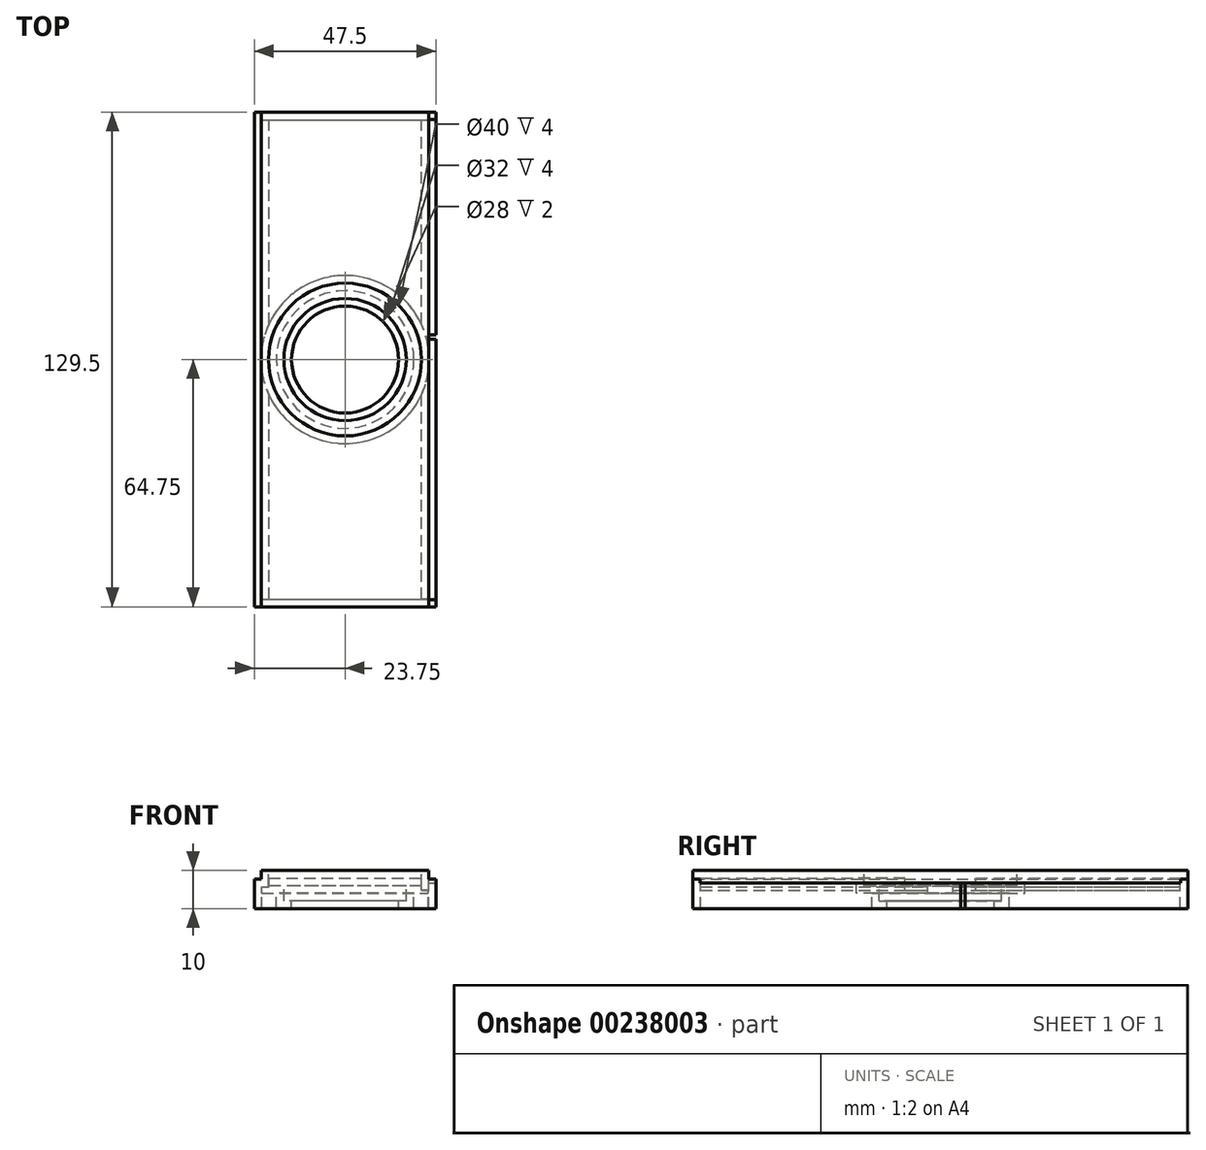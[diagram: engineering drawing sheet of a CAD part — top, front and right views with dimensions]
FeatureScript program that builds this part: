
annotation { "Feature Type Name" : "Feature", "Feature Type Description" : "" }
export const myFeature = defineFeature(function(context is Context, id is Id, definition is map)
    precondition{}
    {
        {
            var Q0;
            Q0=qCreatedBy(makeId("Front.planeOp"),FACE);
            var sketch = newSketch(context, id + "F0", { "sketchPlane" : qUnion([Q0])});
            skLineSegment(sketch, "E0.bottom", {"start": v(-23.75, 0) * mm, "end": v(23.75, 0) * mm});
            skLineSegment(sketch, "E0.top", {"start": v(-23.75, 7.75) * mm, "end": v(-21.95, 7.75) * mm});
            skLineSegment(sketch, "E0.left", {"start": v(-23.75, 0) * mm, "end": v(-23.75, 7.75) * mm});
            skLineSegment(sketch, "E0.right", {"start": v(23.75, 0) * mm, "end": v(23.75, 7.75) * mm});
            skLineSegment(sketch, "E1.top", {"start": v(-21.95, 10) * mm, "end": v(21.95, 10) * mm});
            skLineSegment(sketch, "E1.left", {"start": v(-21.95, 7.75) * mm, "end": v(-21.95, 10) * mm});
            skLineSegment(sketch, "E1.right", {"start": v(21.95, 7.75) * mm, "end": v(21.95, 10) * mm});
            skLineSegment(sketch, "E2.trimOffspring", {"start": v(21.95, 7.75) * mm, "end": v(23.75, 7.75) * mm});
            skSolve(sketch);
        }
        {
            var Q0;
            Q0 = qSketchRegion(id + "F0", true);
            extrude(context, id + "F1", {"entities" : qUnion([Q0]), "endBound" : BoundingType.SYMMETRIC, "depth" : 129.5 * mm});
        }
        {
            var Q0;
            Q0=makeQuery(id+"F1.opExtrude","SWEPT_FACE",FACE,{"disambiguationData":[OSD([sQuery(id+"F0.wireOp",EDGE,"E2.trimOffspring")])]});
            var sketch = newSketch(context, id + "F2", { "sketchPlane" : qUnion([Q0])});
            skLineSegment(sketch, "E3.bottom", {"start": v(23.75, -62.85) * mm, "end": v(21.95, -62.85) * mm});
            skLineSegment(sketch, "E3.top", {"start": v(23.75, 62.85) * mm, "end": v(21.95, 62.85) * mm});
            skLineSegment(sketch, "E3.left", {"start": v(23.75, -62.85) * mm, "end": v(23.75, 62.85) * mm});
            skLineSegment(sketch, "E3.right", {"start": v(21.95, -62.85) * mm, "end": v(21.95, 62.85) * mm});
            skSolve(sketch);
        }
        {
            var Q0;
            Q0 = qSketchRegion(id + "F2", true);
            extrude(context, id + "F3", {"entities" : qUnion([Q0]), "operationType" : NewBodyOperationType.REMOVE, "oppositeDirection" : true, "depth" : 1 * mm});
        }
        {
            var Q0;
            Q0=makeQuery(id+"F1.opExtrude","SWEPT_FACE",FACE,{"disambiguationData":[OSD([sQuery(id+"F0.wireOp",EDGE,"E1.top")])]});
            var sketch = newSketch(context, id + "F4", { "sketchPlane" : qUnion([Q0])});
            skCircle(sketch, "E4", {"center": v(0, 0) * mm, "radius": 20 * mm});
            skSolve(sketch);
        }
        {
            var Q0;
            Q0 = qSketchRegion(id + "F4", true);
            extrude(context, id + "F5", {"entities" : qUnion([Q0]), "operationType" : NewBodyOperationType.REMOVE, "oppositeDirection" : true, "depth" : 4 * mm});
        }
        {
            var Q0;
            Q0=makeQuery(id+"F5.boolean.opBoolean","COPY",FACE,{"derivedFrom":makeQuery(id+"F5.opExtrude","CAP_FACE",FACE,{"disambiguationData":[OSD([sQuery(id+"F4.wireOp",EDGE,"E4")])],"isStart":false})});
            var sketch = newSketch(context, id + "F6", { "sketchPlane" : qUnion([Q0])});
            skCircle(sketch, "E5", {"center": v(0, 0) * mm, "radius": 16 * mm});
            skSolve(sketch);
        }
        {
            var Q0;
            Q0 = qSketchRegion(id + "F6", true);
            extrude(context, id + "F7", {"entities" : qUnion([Q0]), "operationType" : NewBodyOperationType.REMOVE, "oppositeDirection" : true, "depth" : 4 * mm});
        }
        {
            var Q0;
            Q0=makeQuery(id+"F7.boolean.opBoolean","COPY",FACE,{"derivedFrom":makeQuery(id+"F7.opExtrude","CAP_FACE",FACE,{"disambiguationData":[OSD([sQuery(id+"F6.wireOp",EDGE,"E5")])],"isStart":false})});
            var sketch = newSketch(context, id + "F8", { "sketchPlane" : qUnion([Q0])});
            skCircle(sketch, "E6", {"center": v(0, 0) * mm, "radius": 14 * mm});
            skSolve(sketch);
        }
        {
            var Q0;
            Q0 = qSketchRegion(id + "F8", true);
            extrude(context, id + "F9", {"entities" : qUnion([Q0]), "operationType" : NewBodyOperationType.REMOVE, "endBound" : BoundingType.THROUGH_ALL, "oppositeDirection" : true, "depth" : 25 * mm});
        }
        {
            var Q0;
            Q0=makeQuery(id+"F1.opExtrude","SWEPT_FACE",FACE,{"disambiguationData":[OSD([sQuery(id+"F0.wireOp",EDGE,"E0.bottom")])]});
            shell(context, id + "F10", {"entities" : qUnion([Q0]), "thickness" : 2 * mm});
        }
        {
            var Q0;
            Q0=makeQuery(id+"F1.opExtrude","SWEPT_FACE",FACE,{"disambiguationData":[OSD([sQuery(id+"F0.wireOp",EDGE,"E0.right")])]});
            var sketch = newSketch(context, id + "F11", { "sketchPlane" : qUnion([Q0])});
            skLineSegment(sketch, "E7.bottom", {"start": v(5.35, 0) * mm, "end": v(6.45, 0) * mm});
            skLineSegment(sketch, "E7.top", {"start": v(5.35, 6.75) * mm, "end": v(6.45, 6.75) * mm});
            skLineSegment(sketch, "E7.left", {"start": v(5.35, 0) * mm, "end": v(5.35, 6.75) * mm});
            skLineSegment(sketch, "E7.right", {"start": v(6.45, 0) * mm, "end": v(6.45, 6.75) * mm});
            skSolve(sketch);
        }
        {
            var Q0;
            Q0 = qSketchRegion(id + "F11", true);
            extrude(context, id + "F12", {"entities" : qUnion([Q0]), "operationType" : NewBodyOperationType.REMOVE, "oppositeDirection" : true, "depth" : 1.9 * mm});
        }
    });
